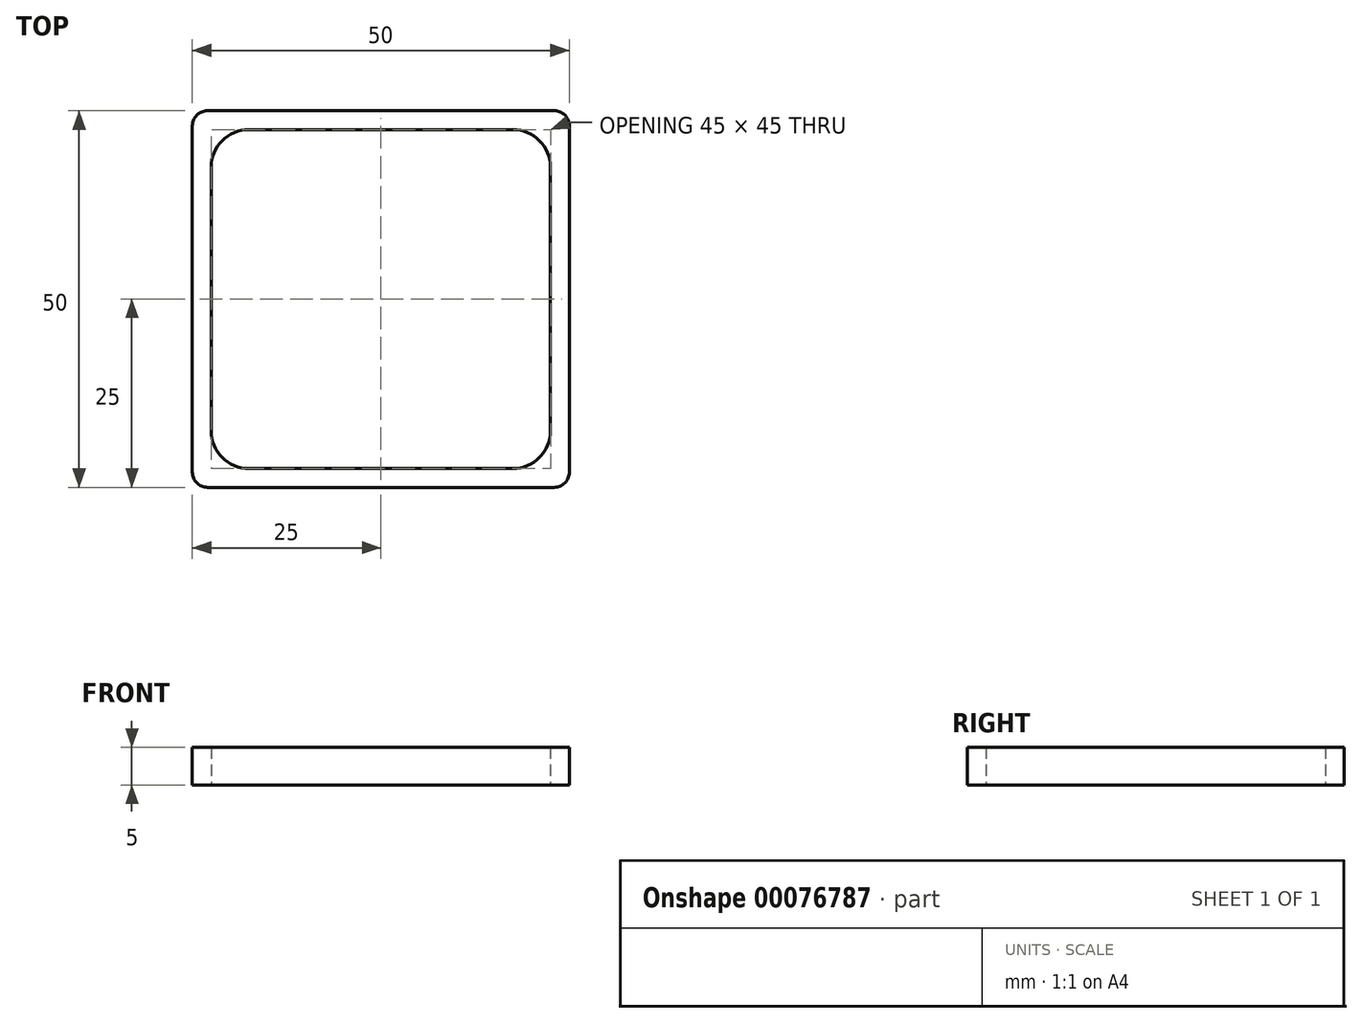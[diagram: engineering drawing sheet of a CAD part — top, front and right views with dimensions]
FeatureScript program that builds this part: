
annotation { "Feature Type Name" : "Feature", "Feature Type Description" : "" }
export const myFeature = defineFeature(function(context is Context, id is Id, definition is map)
    precondition{}
    {
        {
            var Q0;
            Q0=qCreatedBy(makeId("Top.planeOp"),FACE);
            var sketch = newSketch(context, id + "F0", { "sketchPlane" : qUnion([Q0])});
            skLineSegment(sketch, "E0.bottom", {"start": v(-25, 25) * mm, "end": v(25, 25) * mm});
            skLineSegment(sketch, "E0.top", {"start": v(-25, -25) * mm, "end": v(25, -25) * mm});
            skLineSegment(sketch, "E0.left", {"start": v(-25, 25) * mm, "end": v(-25, -25) * mm});
            skLineSegment(sketch, "E0.right", {"start": v(25, 25) * mm, "end": v(25, -25) * mm});
            skLineSegment(sketch, "E1.bottom", {"start": v(-17.5, 22.5) * mm, "end": v(17.5, 22.5) * mm});
            skLineSegment(sketch, "E1.top", {"start": v(-17.5, -22.5) * mm, "end": v(17.5, -22.5) * mm});
            skLineSegment(sketch, "E1.left", {"start": v(-22.5, 17.5) * mm, "end": v(-22.5, -17.5) * mm});
            skLineSegment(sketch, "E1.right", {"start": v(22.5, 17.5) * mm, "end": v(22.5, -17.5) * mm});
            skPoint(sketch, "E2.visualSharp", {"position": v(-22.5, -22.5) * mm});
            skArc(sketch, "E2.filletArc", {"start": v(-22.5, -17.5) * mm, "mid": v(-21.04, -21.04) * mm, "end": v(-17.5, -22.5) * mm});
            skPoint(sketch, "E3.visualSharp", {"position": v(-22.5, 22.5) * mm});
            skArc(sketch, "E3.filletArc", {"start": v(-17.5, 22.5) * mm, "mid": v(-21.04, 21.04) * mm, "end": v(-22.5, 17.5) * mm});
            skPoint(sketch, "E4.visualSharp", {"position": v(22.5, 22.5) * mm});
            skArc(sketch, "E4.filletArc", {"start": v(22.5, 17.5) * mm, "mid": v(21.04, 21.04) * mm, "end": v(17.5, 22.5) * mm});
            skPoint(sketch, "E5.visualSharp", {"position": v(22.5, -22.5) * mm});
            skArc(sketch, "E5.filletArc", {"start": v(17.5, -22.5) * mm, "mid": v(21.04, -21.04) * mm, "end": v(22.5, -17.5) * mm});
            skSolve(sketch);
        }
        {
            var Q0;
            Q0=makeQuery(id+"F0.imprint","IMPRINT",FACE,{"disambiguationData":[TD([[makeQuery(id+"F0.imprint","IMPRINT",EDGE,{"derivedFrom":sQuery(id+"F0.wireOp",EDGE,"E0.bottom")}),-1.0]])]});
            extrude(context, id + "F1", {"entities" : qUnion([Q0]), "depth" : 5 * mm});
        }
        {
            var Q0;
            Q0=makeQuery(id+"F1.opExtrude","SWEPT_EDGE",EDGE,{"disambiguationData":[OSD([sQuery(id+"F0.wireOp",EDGE,"E0.top"),sQuery(id+"F0.wireOp",EDGE,"E0.left")])]});
            var Q1;
            Q1=makeQuery(id+"F1.opExtrude","SWEPT_EDGE",EDGE,{"disambiguationData":[OSD([sQuery(id+"F0.wireOp",EDGE,"E0.top"),sQuery(id+"F0.wireOp",EDGE,"E0.right")])]});
            var Q2;
            Q2=makeQuery(id+"F1.opExtrude","SWEPT_EDGE",EDGE,{"disambiguationData":[OSD([sQuery(id+"F0.wireOp",EDGE,"E0.bottom"),sQuery(id+"F0.wireOp",EDGE,"E0.right")])]});
            var Q3;
            Q3=makeQuery(id+"F1.opExtrude","SWEPT_EDGE",EDGE,{"disambiguationData":[OSD([sQuery(id+"F0.wireOp",EDGE,"E0.bottom"),sQuery(id+"F0.wireOp",EDGE,"E0.left")])]});
            fillet(context, id + "F2", {"entities" : qUnion([Q0, Q1, Q2, Q3]), "radius" : 2 * mm, "tangentPropagation" : true, "allowEdgeOverflow" : false});
        }
    });
